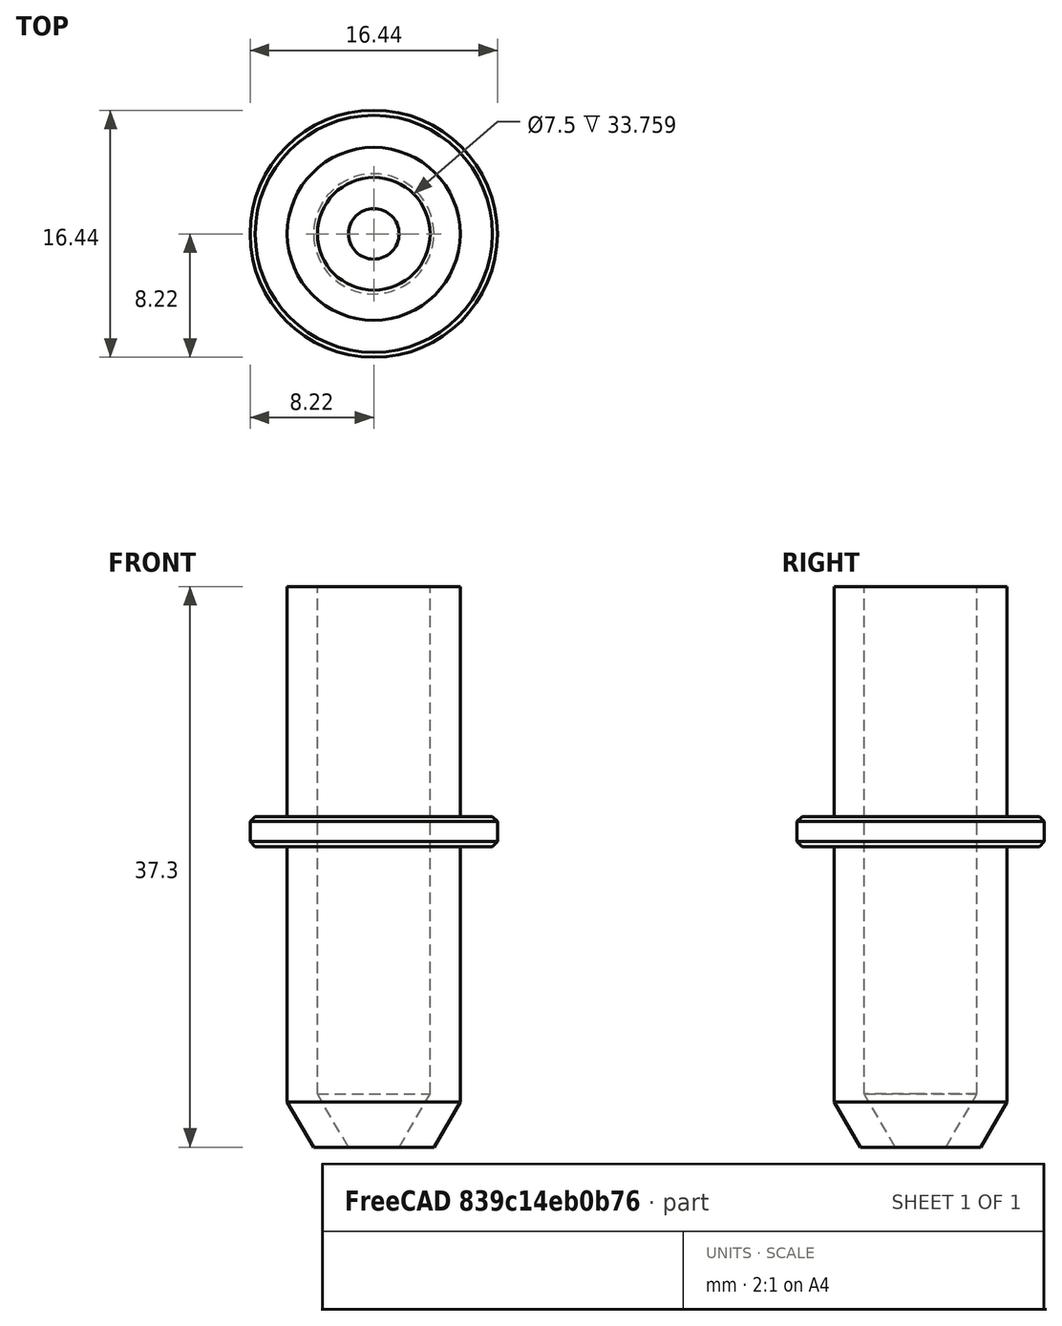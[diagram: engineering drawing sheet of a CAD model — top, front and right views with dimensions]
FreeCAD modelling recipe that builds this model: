
FCSTD DOCUMENT  (FreeCAD 0.18R16110 (Git))
Label: Plotter-Stift
License: All rights reserved
LicenseURL: http://en.wikipedia.org/wiki/All_rights_reserved
objects: Sketcher::SketchObject×1, PartDesign::Revolution×1, PartDesign::Body×1
note: 4 computed .brp shape members not serialized (recipe doc carries the construction recipe); baked Part::Feature solids carry a one-line shape summary decoded from their .brp

FEATURE [Sketcher::SketchObject] Sketch
  MapMode = 5
  Placement = pos=(0,0,0) rot=(1,0,0;1.5708rad)
  Support = -> [XZ_Plane]
  sketch-geometry (14):
    g0: LineSegment StartX=-1.68459 StartY=0 StartZ=0 EndX=-3.75 EndY=3.5407 EndZ=0
    g1: LineSegment StartX=-3.75 StartY=3.5407 StartZ=0 EndX=-3.75 EndY=37.3 EndZ=0
    g2: LineSegment StartX=-3.75 StartY=37.3 StartZ=0 EndX=-5.75 EndY=37.3 EndZ=0
    g3: LineSegment StartX=-5.75 StartY=37.3 StartZ=0 EndX=-5.75 EndY=22 EndZ=0
    g4: LineSegment StartX=-5.75 StartY=22 StartZ=0 EndX=-7.885 EndY=22 EndZ=0
    g5: LineSegment StartX=-8.22 StartY=21.665 StartZ=0 EndX=-8.22 EndY=20.335 EndZ=0
    g6: LineSegment StartX=-7.885 StartY=20 StartZ=0 EndX=-5.75 EndY=20 EndZ=0
    g7: LineSegment StartX=-8.22 StartY=21.665 StartZ=0 EndX=-7.885 EndY=22 EndZ=0
    g8: LineSegment StartX=-8.22 StartY=20.335 StartZ=0 EndX=-7.885 EndY=20 EndZ=0
    g9: LineSegment StartX=-5.75 StartY=20 StartZ=0 EndX=-5.75 EndY=3 EndZ=0
    g10: LineSegment StartX=-5.75 StartY=3 StartZ=0 EndX=-4 EndY=0 EndZ=0
    g11: LineSegment StartX=-4 StartY=0 StartZ=0 EndX=-1.68459 EndY=0 EndZ=0
    g12: GeomPoint X=-5.47756 Y=2.53296 Z=0
    g13: LineSegment [constr] StartX=-5.47756 StartY=2.53296 StartZ=0 EndX=-3.75 EndY=3.5407 EndZ=0
  constraints (41):
    c: Coincident(g0,g1)
    c: Vertical(g1)
    c: Coincident(g2,g1)
    c: Horizontal(g2)
    c: Vertical(g3)
    c: Coincident(g4,g3)
    c: Horizontal(g4)
    c: Vertical(g5)
    c: Horizontal(g6)
    c: Coincident(g7,g4)
    c: Coincident(g5,g7)
    c: Coincident(g8,g5)
    c: Coincident(g8,g6)
    c: Equal(g6,g4)
    c: Angle(g5,g7) = 2.35619
    c: Equal(g7,g8)
    c: Coincident(g9,g6)
    c: Vertical(g9)
    c: Coincident(g3,g2)
    c: Equal(g6,g4)
    c: Angle(g8,g5) = 2.35619
    c: DistanceY(g6,g3) = 2  'ringwidth'
    c: DistanceY(g5,g5) = 1.33
    c: DistanceX(g2,g-1) = 5.75
    c: DistanceX(g2,g1) = 2
    c: DistanceY(g-1,g2) = 37.3
    c: Coincident(g11,g0)
    c: Coincident(g11,g10)
    c: Horizontal(g11)
    c: DistanceY(g0,g-1) = 0
    c: Coincident(g10,g9)
    c: Parallel(g10,g0)
    c: DistanceY(g-1,g6) = 20
    c: PointOnObject(g12,g10)
    c: Distance(g12,g0) = 2
    c: Perpendicular(g13,g10)
    c: Coincident(g13,g12)
    c: Coincident(g13,g0)
    c: DistanceY(g-1,g9) = 3
    c: DistanceX(g10,g-1) = 4
    c: DistanceX(g5,g-1) = 8.22
FEATURE [PartDesign::Revolution] Revolution
  Angle = 360
  Axis = (0,2e-16,1)
  Base = (0,0,0)
  Placement = pos=(0,0,0) rot=(1,0,0;1.5708rad)
  Profile = -> Sketch
  ReferenceAxis = -> Sketch [V_Axis]
FEATURE [PartDesign::Body] Body
  Group = -> [Sketch,Revolution]
  Origin = -> Origin
  Tip = -> Revolution
